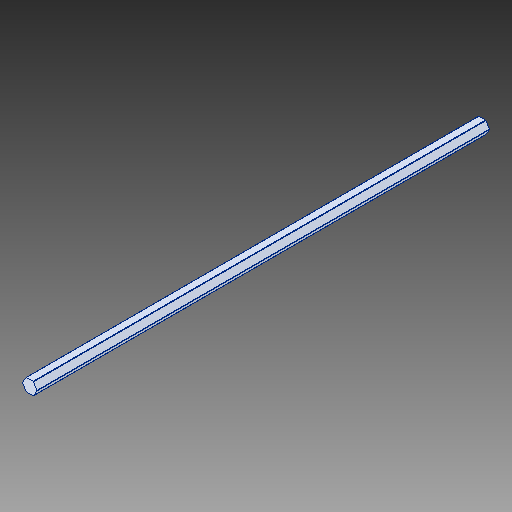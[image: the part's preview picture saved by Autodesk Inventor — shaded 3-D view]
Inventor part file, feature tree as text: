
AUTODESK INVENTOR PART (.ipt)
format: ipt  version: 2017 (Build 210142000, 142)  size: 99,328 bytes
history: native  units: in
note: dims shown in document units (in); Inventor stores cm internally (conversion verified against a paired STEP export)
features: fillet x1
ambient origin geometry x8: Origin, YZ Plane, XZ Plane, XY Plane, X Axis, Y Axis, Z Axis, Center Point
bodies: Solid1 (feature_tree)
feature tree (1):
  fillet  "Fillet1"  [1 undecoded]
note: 1 required parameter value undecoded (feature->parameter linkage not recoverable at this tier; creation-order binding heuristic only, values carry confidence <= 0.55)
